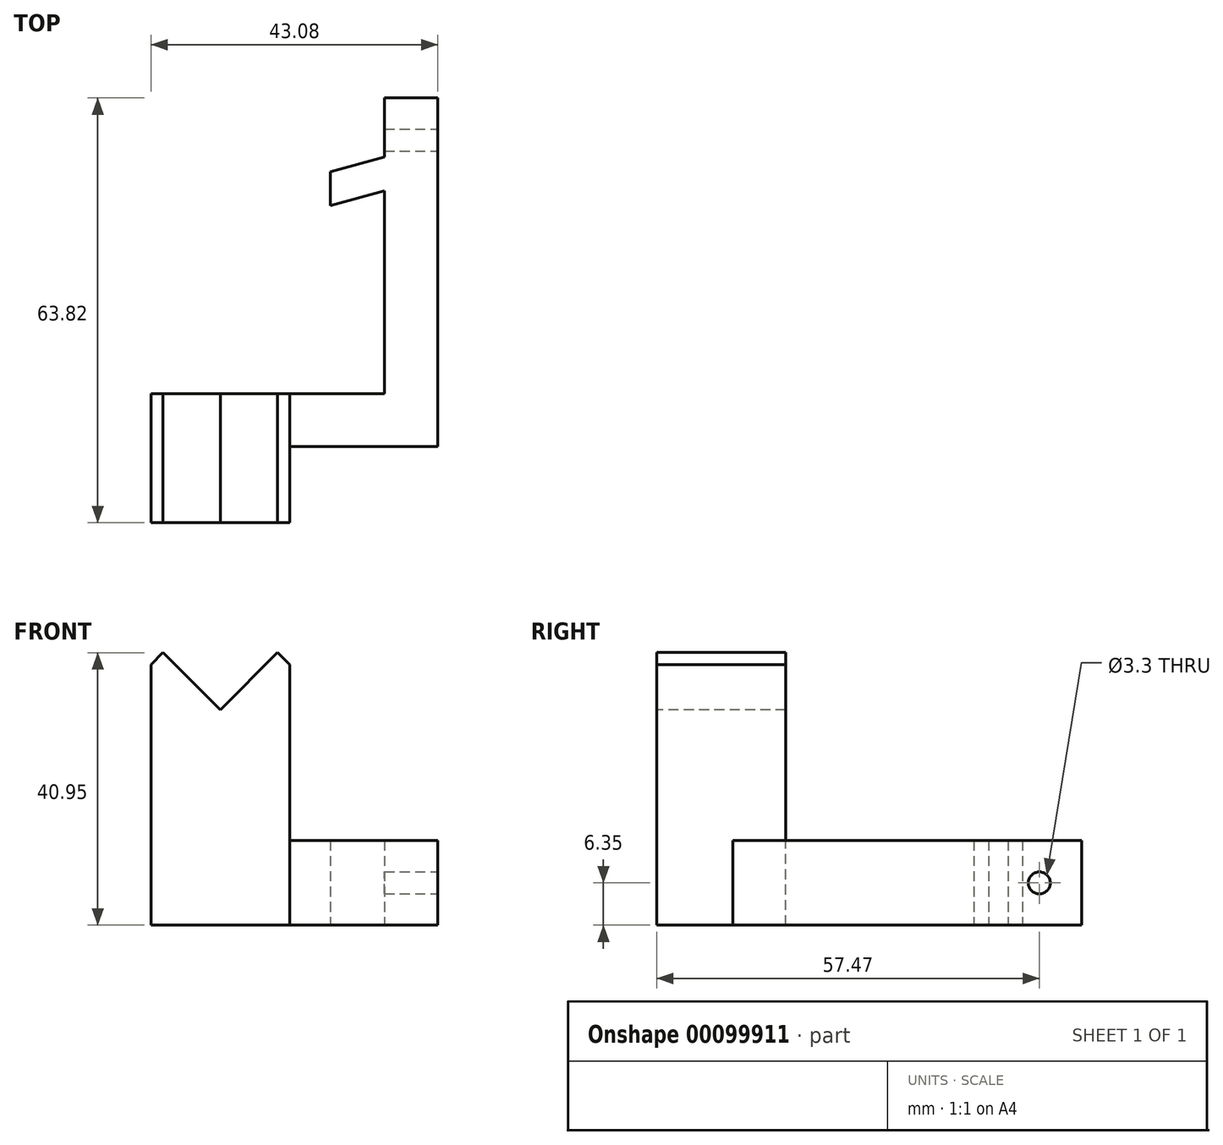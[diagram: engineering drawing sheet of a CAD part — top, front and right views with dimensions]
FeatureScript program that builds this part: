
annotation { "Feature Type Name" : "Feature", "Feature Type Description" : "" }
export const myFeature = defineFeature(function(context is Context, id is Id, definition is map)
    precondition{}
    {
        {
            var Q0;
            Q0=qCreatedBy(makeId("Right.planeOp"),FACE);
            var sketch = newSketch(context, id + "F0", { "sketchPlane" : qUnion([Q0])});
            skLineSegment(sketch, "E0.bottom", {"start": v(0, 0) * mm, "end": v(-44.45, 0) * mm});
            skLineSegment(sketch, "E0.top", {"start": v(0, 12.7) * mm, "end": v(-44.45, 12.7) * mm});
            skLineSegment(sketch, "E0.left", {"start": v(0, 0) * mm, "end": v(0, 12.7) * mm});
            skLineSegment(sketch, "E0.right", {"start": v(-44.45, 0) * mm, "end": v(-44.45, 12.7) * mm});
            skSolve(sketch);
        }
        {
            var Q0;
            Q0 = qSketchRegion(id + "F0", true);
            extrude(context, id + "F1", {"entities" : qUnion([Q0]), "depth" : 8 * mm});
        }
        {
            var Q0;
            Q0=makeQuery(id+"F1.opExtrude","SWEPT_FACE",FACE,{"disambiguationData":[OSD([sQuery(id+"F0.wireOp",EDGE,"E0.right")])]});
            var sketch = newSketch(context, id + "F2", { "sketchPlane" : qUnion([Q0])});
            skLineSegment(sketch, "E1.bottom", {"start": v(0, 12.7) * mm, "end": v(-35.08, 12.7) * mm});
            skLineSegment(sketch, "E1.top", {"start": v(0, 0) * mm, "end": v(-35.08, 0) * mm});
            skLineSegment(sketch, "E1.right", {"start": v(-35.08, 12.7) * mm, "end": v(-35.08, 0) * mm});
            skLineSegment(sketch, "E2.bottom", {"start": v(0, 12.7) * mm, "end": v(8, 12.7) * mm});
            skLineSegment(sketch, "E2.top", {"start": v(0, 0) * mm, "end": v(8, 0) * mm});
            skLineSegment(sketch, "E2.right", {"start": v(8, 12.7) * mm, "end": v(8, 0) * mm});
            skSolve(sketch);
        }
        {
            var Q0;
            Q0 = qSketchRegion(id + "F2", true);
            extrude(context, id + "F3", {"entities" : qUnion([Q0]), "operationType" : NewBodyOperationType.ADD, "depth" : 7.94 * mm});
        }
        {
            var Q0;
            Q0=makeQuery(id+"F3.opExtrude","CAP_FACE",FACE,{"disambiguationData":[OSD([sQuery(id+"F2.wireOp",EDGE,"E1.bottom"),sQuery(id+"F2.wireOp",EDGE,"E1.top"),sQuery(id+"F2.wireOp",EDGE,"E1.right"),sQuery(id+"F2.wireOp",EDGE,"E2.bottom"),sQuery(id+"F2.wireOp",EDGE,"E2.top"),sQuery(id+"F2.wireOp",EDGE,"E2.right")])],"isStart":false});
            var sketch = newSketch(context, id + "F4", { "sketchPlane" : qUnion([Q0])});
            skLineSegment(sketch, "E3", {"start": v(-35.08, 0) * mm, "end": v(-14.25, 0) * mm});
            skLineSegment(sketch, "E4", {"start": v(-14.25, 0) * mm, "end": v(-14.25, 39.16) * mm});
            skLineSegment(sketch, "E5", {"start": v(-14.25, 39.16) * mm, "end": v(-14.25, 39.16) * mm});
            skLineSegment(sketch, "E6", {"start": v(-14.25, 39.16) * mm, "end": v(-16.05, 40.95) * mm});
            skLineSegment(sketch, "E7", {"start": v(-16.05, 40.95) * mm, "end": v(-24.67, 32.33) * mm});
            skLineSegment(sketch, "E8", {"start": v(-24.67, 32.33) * mm, "end": v(-33.29, 40.95) * mm});
            skLineSegment(sketch, "E9", {"start": v(-33.29, 40.95) * mm, "end": v(-35.08, 39.16) * mm});
            skLineSegment(sketch, "E10", {"start": v(-35.08, 39.16) * mm, "end": v(-35.08, 39.16) * mm});
            skLineSegment(sketch, "E11", {"start": v(-35.08, 39.16) * mm, "end": v(-35.08, 0) * mm});
            skPoint(sketch, "E12", {"position": v(-24.67, 0) * mm});
            skCircle(sketch, "E13", {"center": v(-24.67, 38.08) * mm, "radius": 4.06 * mm, "construction": true});
            skSolve(sketch);
        }
        {
            var Q0;
            Q0 = qSketchRegion(id + "F4", true);
            var Q1;
            Q1=makeQuery(id+"F3.opExtrude","CAP_FACE",FACE,{"disambiguationData":[OSD([sQuery(id+"F2.wireOp",EDGE,"E1.bottom"),sQuery(id+"F2.wireOp",EDGE,"E1.top"),sQuery(id+"F2.wireOp",EDGE,"E1.right"),sQuery(id+"F2.wireOp",EDGE,"E2.bottom"),sQuery(id+"F2.wireOp",EDGE,"E2.top"),sQuery(id+"F2.wireOp",EDGE,"E2.right")])],"isStart":true});
            extrude(context, id + "F5", {"entities" : qUnion([Q0]), "operationType" : NewBodyOperationType.ADD, "endBound" : BoundingType.UP_TO_SURFACE, "oppositeDirection" : true, "endBoundEntityFace" : qUnion([Q1]), "depth" : 25.4 * mm, "hasSecondDirection" : true, "secondDirectionOppositeDirection" : false, "secondDirectionDepth" : 11.43 * mm});
        }
        {
            var Q0;
            Q0=makeQuery(id+"F3.boolean.opBoolean","MERGE",FACE,{"derivedFrom":[makeQuery(id+"F1.opExtrude","CAP_FACE",FACE,{"disambiguationData":[OSD([sQuery(id+"F0.wireOp",EDGE,"E0.bottom"),sQuery(id+"F0.wireOp",EDGE,"E0.top"),sQuery(id+"F0.wireOp",EDGE,"E0.left"),sQuery(id+"F0.wireOp",EDGE,"E0.right")])],"isStart":false}),makeQuery(id+"F3.opExtrude","SWEPT_FACE",FACE,{"disambiguationData":[OSD([sQuery(id+"F2.wireOp",EDGE,"E2.right")])]})]});
            var sketch = newSketch(context, id + "F6", { "sketchPlane" : qUnion([Q0])});
            skCircle(sketch, "E14", {"center": v(-6.35, 6.35) * mm, "radius": 1.65 * mm});
            skPoint(sketch, "E14.centerSnap0", {"position": v(0, 6.35) * mm});
            skSolve(sketch);
        }
        {
            var Q0;
            Q0 = qSketchRegion(id + "F6", true);
            extrude(context, id + "F7", {"entities" : qUnion([Q0]), "operationType" : NewBodyOperationType.REMOVE, "oppositeDirection" : true, "depth" : 25.4 * mm});
        }
        {
            var Q0;
            Q0=makeQuery(id+"F5.boolean.opBoolean","MERGE",FACE,{"derivedFrom":[makeQuery(id+"F3.boolean.opBoolean","MERGE",FACE,{"derivedFrom":[makeQuery(id+"F1.opExtrude","SWEPT_FACE",FACE,{"disambiguationData":[OSD([sQuery(id+"F0.wireOp",EDGE,"E0.bottom")])]}),makeQuery(id+"F3.opExtrude","SWEPT_FACE",FACE,{"disambiguationData":[OSD([sQuery(id+"F2.wireOp",EDGE,"E1.top"),sQuery(id+"F2.wireOp",EDGE,"E2.top")])]})]}),makeQuery(id+"F5.opExtrude","SWEPT_FACE",FACE,{"disambiguationData":[OSD([sQuery(id+"F4.wireOp",EDGE,"E3")])]})]});
            var sketch = newSketch(context, id + "F8", { "sketchPlane" : qUnion([Q0])});
            skLineSegment(sketch, "E15", {"start": v(0, 8.9) * mm, "end": v(-8.17, 11.08) * mm});
            skLineSegment(sketch, "E16", {"start": v(-8.17, 11.08) * mm, "end": v(-8.17, 16.16) * mm});
            skLineSegment(sketch, "E17", {"start": v(-8.17, 16.16) * mm, "end": v(0, 13.97) * mm});
            skLineSegment(sketch, "E18", {"start": v(0, 8.9) * mm, "end": v(0, 13.97) * mm});
            skSolve(sketch);
        }
        {
            var Q0;
            Q0 = qSketchRegion(id + "F8", true);
            var Q1;
            Q1=makeQuery(id+"F3.boolean.opBoolean","MERGE",FACE,{"derivedFrom":[makeQuery(id+"F1.opExtrude","SWEPT_FACE",FACE,{"disambiguationData":[OSD([sQuery(id+"F0.wireOp",EDGE,"E0.top")])]}),makeQuery(id+"F3.opExtrude","SWEPT_FACE",FACE,{"disambiguationData":[OSD([sQuery(id+"F2.wireOp",EDGE,"E1.bottom"),sQuery(id+"F2.wireOp",EDGE,"E2.bottom")])]})]});
            extrude(context, id + "F9", {"entities" : qUnion([Q0]), "operationType" : NewBodyOperationType.ADD, "endBound" : BoundingType.UP_TO_SURFACE, "oppositeDirection" : true, "endBoundEntityFace" : qUnion([Q1]), "depth" : 25.4 * mm});
        }
    });
